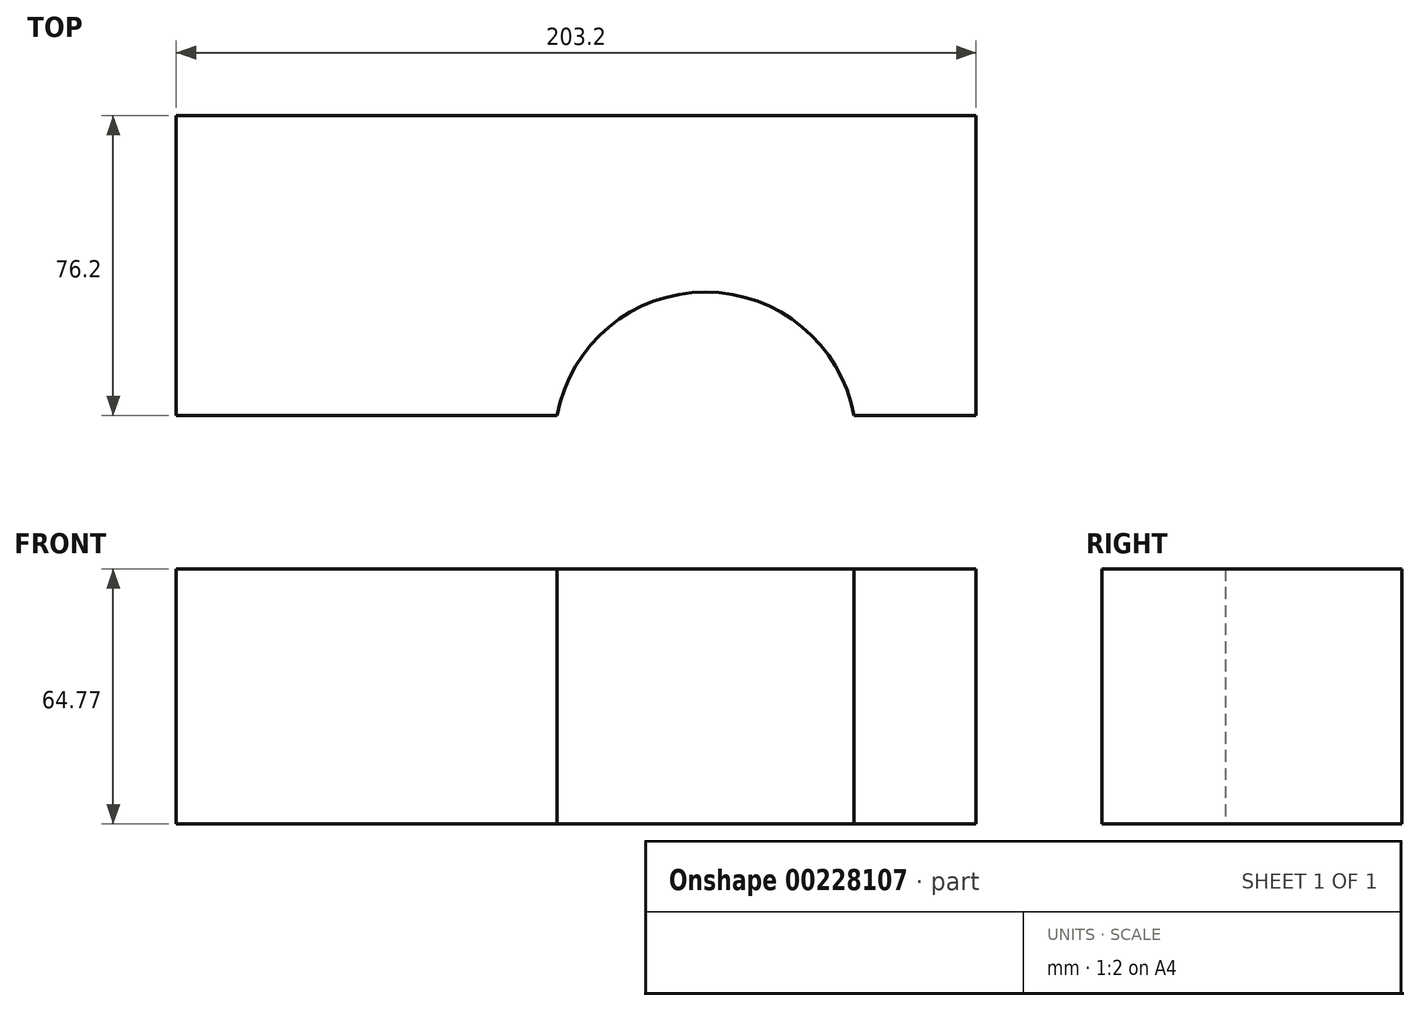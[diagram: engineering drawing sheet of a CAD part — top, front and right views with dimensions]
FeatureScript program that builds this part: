
annotation { "Feature Type Name" : "Feature", "Feature Type Description" : "" }
export const myFeature = defineFeature(function(context is Context, id is Id, definition is map)
    precondition{}
    {
        {
            var Q0;
            Q0=qCreatedBy(makeId("Top.planeOp"),FACE);
            var sketch = newSketch(context, id + "F0", { "sketchPlane" : qUnion([Q0])});
            skLineSegment(sketch, "E0.bottom", {"start": v(-58.59, 70.99) * mm, "end": v(144.61, 70.99) * mm});
            skLineSegment(sketch, "E0.top", {"start": v(-58.59, -5.21) * mm, "end": v(144.61, -5.21) * mm});
            skLineSegment(sketch, "E0.left", {"start": v(-58.59, 70.99) * mm, "end": v(-58.59, -5.21) * mm});
            skLineSegment(sketch, "E0.right", {"start": v(144.61, 70.99) * mm, "end": v(144.61, -5.21) * mm});
            skLineSegment(sketch, "E1", {"start": v(-101.7, -50.53) * mm, "end": v(175.29, -50.53) * mm, "construction": true});
            skCircle(sketch, "E2", {"center": v(75.88, -12.2) * mm, "radius": 38.34 * mm});
            skSolve(sketch);
        }
        {
            var Q0;
            Q0=makeQuery(id+"F0.imprint","IMPRINT",FACE,{"disambiguationData":[TD([[makeQuery(id+"F0.imprint","IMPRINT",EDGE,{"derivedFrom":sQuery(id+"F0.wireOp",EDGE,"E0.bottom")}),-1.0]])]});
            extrude(context, id + "F1", {"entities" : qUnion([Q0]), "depth" : 64.77 * mm});
        }
    });
